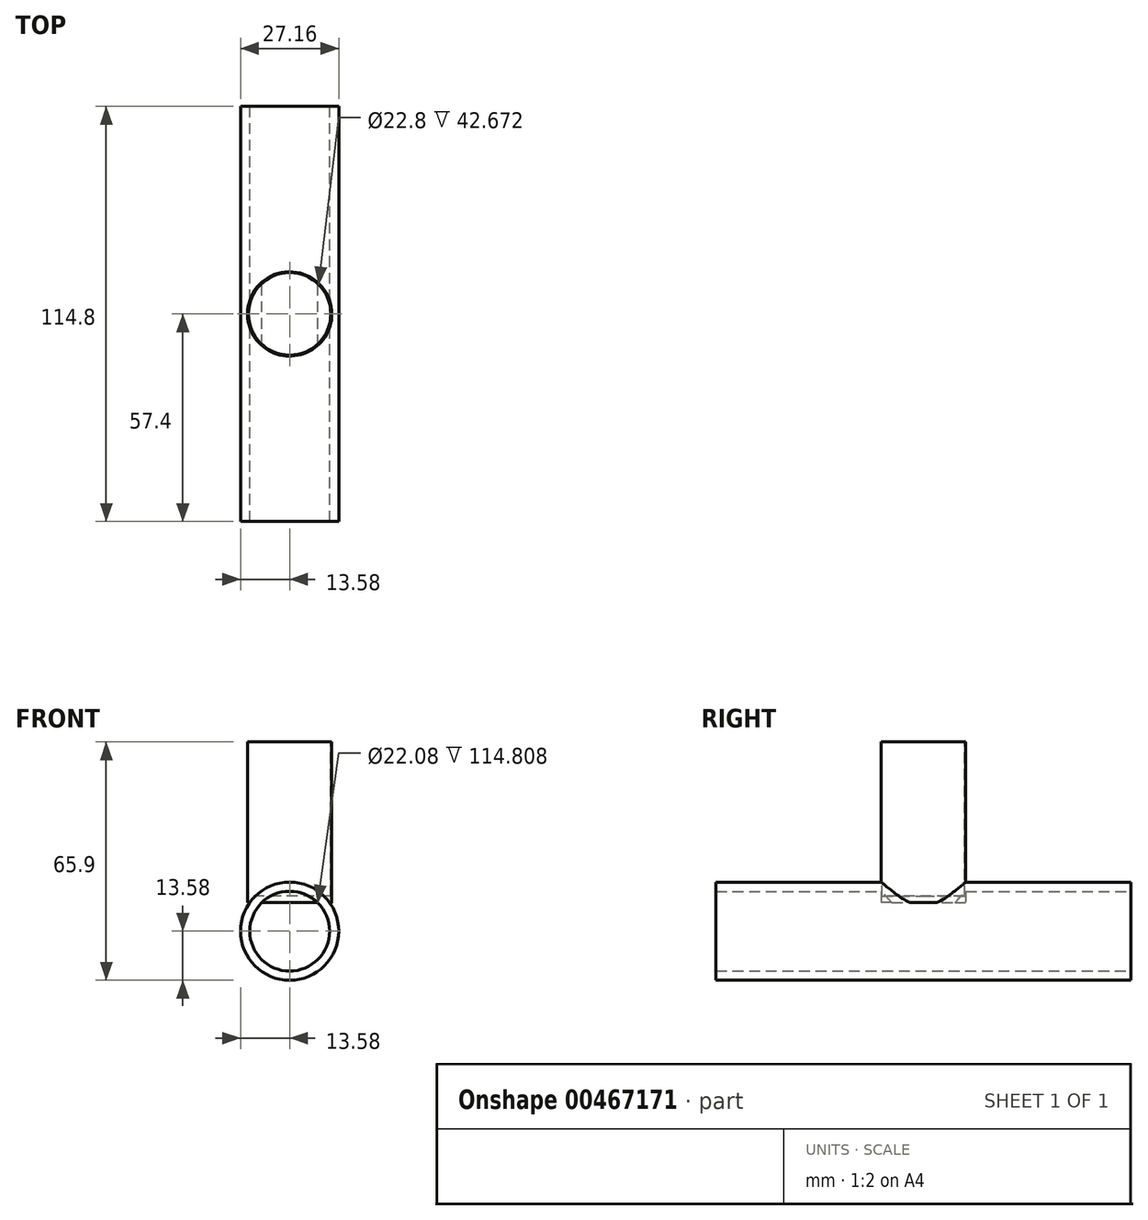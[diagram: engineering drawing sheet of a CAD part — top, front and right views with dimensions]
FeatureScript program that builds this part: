
annotation { "Feature Type Name" : "Feature", "Feature Type Description" : "" }
export const myFeature = defineFeature(function(context is Context, id is Id, definition is map)
    precondition{}
    {
        {
            var Q0;
            Q0=qCreatedBy(makeId("Front.planeOp"),FACE);
            var sketch = newSketch(context, id + "F0", { "sketchPlane" : qUnion([Q0])});
            skCircle(sketch, "E0", {"center": v(0, 0) * mm, "radius": 13.58 * mm});
            skSolve(sketch);
        }
        {
            var Q0;
            Q0 = qSketchRegion(id + "F0", true);
            extrude(context, id + "F1", {"entities" : qUnion([Q0]), "endBound" : BoundingType.SYMMETRIC, "depth" : 114.8 * mm});
        }
        {
            var Q0;
            Q0=makeQuery(id+"F1.opExtrude","CAP_FACE",FACE,{"disambiguationData":[OSD([sQuery(id+"F0.wireOp",EDGE,"E0")])],"isStart":false});
            var Q1;
            Q1=makeQuery(id+"F1.opExtrude","CAP_FACE",FACE,{"disambiguationData":[OSD([sQuery(id+"F0.wireOp",EDGE,"E0")])],"isStart":true});
            shell(context, id + "F2", {"entities" : qUnion([Q0, Q1]), "thickness" : 2.54 * mm});
        }
        {
            var Q0;
            Q0=qCreatedBy(makeId("Top.planeOp"),FACE);
            cPlane(context, id + "F3", {"entities" : qUnion([Q0]), "cplaneType" : CPlaneType.OFFSET, "offset" : 7.87 * mm, "width" : 152.4 * mm, "height" : 152.4 * mm});
        }
        {
            var Q0;
            Q0=qCreatedBy(id+"F3.planeOp",FACE);
            var sketch = newSketch(context, id + "F4", { "sketchPlane" : qUnion([Q0])});
            skCircle(sketch, "E1", {"center": v(0, 0) * mm, "radius": 11.67 * mm});
            skSolve(sketch);
        }
        {
            var Q0;
            Q0 = qSketchRegion(id + "F4", true);
            extrude(context, id + "F5", {"entities" : qUnion([Q0]), "operationType" : NewBodyOperationType.ADD, "depth" : 44.45 * mm});
        }
        {
            var Q0;
            Q0=makeQuery(id+"F5.opExtrude","CAP_FACE",FACE,{"disambiguationData":[OSD([sQuery(id+"F4.wireOp",EDGE,"E1")])],"isStart":false});
            var sketch = newSketch(context, id + "F6", { "sketchPlane" : qUnion([Q0])});
            skCircle(sketch, "E2", {"center": v(0, 0) * mm, "radius": 11.4 * mm});
            skSolve(sketch);
        }
        {
            var Q0;
            Q0=makeQuery(id+"F6.imprint","IMPRINT",FACE,{"disambiguationData":[TD([[makeQuery(id+"F6.imprint","IMPRINT",EDGE,{"derivedFrom":sQuery(id+"F6.wireOp",EDGE,"E2")}),1.0]])]});
            extrude(context, id + "F7", {"entities" : qUnion([Q0]), "operationType" : NewBodyOperationType.REMOVE, "oppositeDirection" : true, "depth" : 42.67 * mm});
        }
    });
